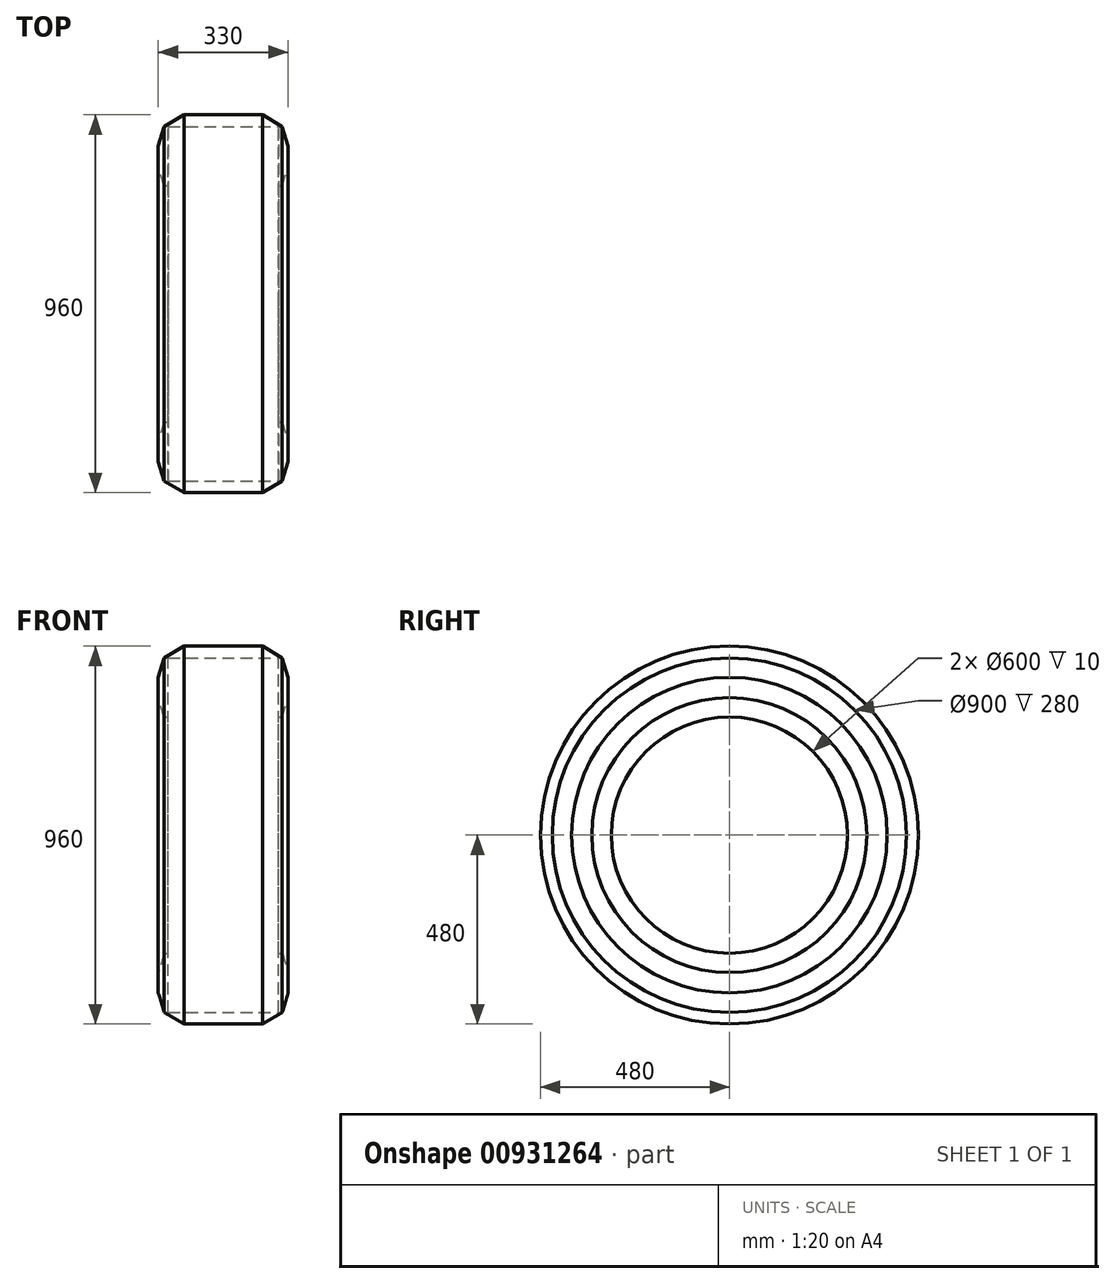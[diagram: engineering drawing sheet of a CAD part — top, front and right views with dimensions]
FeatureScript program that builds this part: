
annotation { "Feature Type Name" : "Feature", "Feature Type Description" : "" }
export const myFeature = defineFeature(function(context is Context, id is Id, definition is map)
    precondition{}
    {
        {
            var Q0;
            Q0=qCreatedBy(makeId("Top.planeOp"),FACE);
            var sketch = newSketch(context, id + "F0", { "sketchPlane" : qUnion([Q0])});
            skLineSegment(sketch, "E0", {"start": v(0, 0) * mm, "end": v(-364.18, 0) * mm, "construction": true});
            skLineSegment(sketch, "E1.top", {"start": v(-150, -450) * mm, "end": v(150, -450) * mm, "construction": true});
            skLineSegment(sketch, "E1.left", {"start": v(-150, -300) * mm, "end": v(-150, -450) * mm, "construction": true});
            skLineSegment(sketch, "E1.right", {"start": v(150, -300) * mm, "end": v(150, -450) * mm, "construction": true});
            skLineSegment(sketch, "E2", {"start": v(-150, -300) * mm, "end": v(-165, -349.26) * mm});
            skLineSegment(sketch, "E3", {"start": v(-165, -349.26) * mm, "end": v(-165, -400.74) * mm});
            skLineSegment(sketch, "E4", {"start": v(-165, -400.74) * mm, "end": v(-150, -450) * mm});
            skLineSegment(sketch, "E5", {"start": v(-150, -450) * mm, "end": v(-100, -480) * mm});
            skLineSegment(sketch, "E6", {"start": v(-100, -480) * mm, "end": v(100, -480) * mm});
            skLineSegment(sketch, "E7", {"start": v(100, -480) * mm, "end": v(150, -450) * mm});
            skLineSegment(sketch, "E8.MirrorCS", {"start": v(150, -300) * mm, "end": v(165, -349.26) * mm});
            skLineSegment(sketch, "E9.MirrorCS", {"start": v(165, -349.26) * mm, "end": v(165, -400.74) * mm});
            skLineSegment(sketch, "E10.MirrorCS", {"start": v(165, -400.74) * mm, "end": v(150, -450) * mm});
            skLineSegment(sketch, "E11", {"start": v(-150, -300) * mm, "end": v(-140, -300) * mm});
            skLineSegment(sketch, "E12", {"start": v(-140, -300) * mm, "end": v(-140, -450) * mm});
            skLineSegment(sketch, "E13", {"start": v(150, -300) * mm, "end": v(140, -300) * mm});
            skLineSegment(sketch, "E14", {"start": v(140, -300) * mm, "end": v(140, -450) * mm});
            skLineSegment(sketch, "E15", {"start": v(140, -450) * mm, "end": v(-140, -450) * mm});
            skSolve(sketch);
        }
        {
            var Q0;
            Q0=makeQuery(id+"F0.imprint","IMPRINT",FACE,{"disambiguationData":[TD([[makeQuery(id+"F0.imprint","IMPRINT",EDGE,{"derivedFrom":sQuery(id+"F0.wireOp",EDGE,"E2")}),1.0]])]});
            var Q1;
            Q1=sQuery(id+"F0.wireOp",EDGE,"E0");
            revolve(context, id + "F1", {"surfaceOperationType" : NewSurfaceOperationType.NEW, "entities" : qUnion([Q0]), "axis" : qUnion([Q1]), "revolveType" : RevolveType.FULL});
        }
    });
